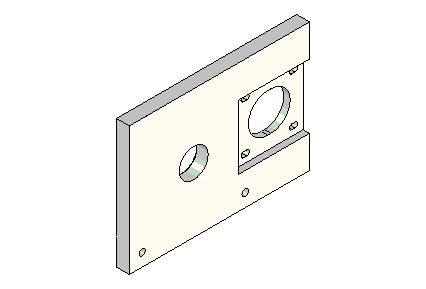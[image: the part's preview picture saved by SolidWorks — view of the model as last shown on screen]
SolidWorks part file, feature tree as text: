
SOLIDWORKS PART (.sldprt)
format: sldprt  version: not decoded by parser v0  size: 434,176 bytes
history: native  units: mm
features: sketch x10, cut_extrude x6, thread x4, extrude x1, hole x1 (+11 scaffold rows collapsed)
feature tree (33):
  scaffold x11  (default folders/planes/origin — collapsed)
  sketch  "Sketch1"  dims[D1=177.8mm D2=127.0mm]
  extrude  "Extrude1"  Depth=12.7mm
  hole  "5/16-18 Tapped Hole1"  Diameter=6.5278mm Depth=22.9235mm
  sketch  "Sketch3"  dims[c1.D1=19.05mm c1.D2=38.1mm c1.D3=38.1mm c1.D4=38.1mm c1.D5=6.35mm c2.D1=31.75mm]
  sketch  "Sketch2"  dims[hole-wizard template sketch: 47 standard entries collapsed; hole parameters kept: c15.Tap Drill Depth=22.9235mm c15.D3=~14.816244mm c15.Drill Angle=118.0deg]
  thread  "Cosmetic Thread1"  Diameter=15.875mm  [1 undecoded]
  thread  "Cosmetic Thread2"  Diameter=15.875mm  [1 undecoded]
  thread  "Cosmetic Thread3"  Diameter=15.875mm  [1 undecoded]
  thread  "Cosmetic Thread4"  Diameter=15.875mm  [1 undecoded]
  sketch  "Sketch4"  dims[c1.D1=115.9256mm c1.D2=31.6992mm c1.D3=30.0736mm c1.D4=25.2222mm c1.D5=64.1604mm c1.D6=57.7088mm c1.D7=57.7088mm c1.D8=30.0736mm c1.D9=30.0736mm c1.D10=64.1604mm c1.D11=64.1604mm c1.D12=25.4mm c1.D13=25.4mm c1.D14=25.4mm c1.D15=25.4mm c1.D16=25.4mm c1.D17=25.4mm c2.D15=25.4mm c2.D11=30.0736mm c2.D18=30.0736mm c2.D19=64.1604mm c2.D2=30.0736mm c2.D5=115.9256mm c2.D7=25.2222mm c2.D8=25.2222mm c2.D9=25.2222mm c2.D6=63.5mm c3.D7=76.2mm c3.D8=30.48mm c3.D9=30.48mm c3.D10=~36.981169mm c3.D11=38.1mm c3.D14=15.875mm c3.D15=25.4mm c3.D16=15.875mm c3.D17=25.4mm c4.D15=25.4mm c4.D11=~78.928619mm c4.D18=79.375mm c4.D19=64.008mm c4.D2=63.5mm c4.D5=82.55mm c4.D7=79.375mm c4.D8=3.175mm c4.D9=63.5mm]
  sketch  "Sketch8"  dims[c1.D3=3.175mm c1.D1=63.5mm c1.D2=63.5mm c2.D1=63.5mm c2.D2=69.85mm c2.D3=63.5mm]
  cut_extrude  "Cut-Extrude2"  Depth=6.35mm
  sketch  "Sketch5"  dims[c1.D1=38.1mm c1.D2=38.1mm c1.D3=38.1mm c2.D2=28.575mm c2.D3=28.575mm]
  cut_extrude  "Cut-Extrude1"  [1 undecoded]
  sketch  "Sketch9"  dims[c1.D1=4.9784mm c1.D3=2.4892mm c1.D4=2.4892mm c1.D2=2.4892mm c2.D3=2.4892mm c2.D4=2.4892mm c2.D5=4.9784mm c2.D6=2.4892mm c2.D7=2.4892mm c2.D8=2.4892mm c2.D9=4.9784mm c2.D10=4.9784mm c2.D11=2.4892mm c2.D12=2.4892mm c2.D13=2.4892mm c2.D14=2.4892mm c2.D15=2.4892mm c2.D16=2.4892mm c2.D2=23.876mm c3.D3=23.876mm c3.D4=23.876mm c3.D2=23.876mm c4.D3=23.876mm c4.D4=23.876mm c4.D6=23.876mm c4.D7=23.876mm c4.D8=23.876mm c4.D11=23.876mm c4.D12=23.876mm c4.D13=23.876mm c4.D14=23.876mm c4.D15=23.876mm c4.D16=23.876mm]
  cut_extrude  "Cut-Extrude4"  [1 undecoded]
  sketch  "Sketch10"  dims[D1=28.575mm]
  cut_extrude  "Cut-Extrude5"  [1 undecoded]
  sketch  "Sketch11"  dims[D1=31.75mm]
  cut_extrude  "Cut-Extrude6"  Depth=1.5875mm
  sketch  "Sketch12"  dims[D1=6.35mm D2=101.6mm D3=12.7mm]
  cut_extrude  "Cut-Extrude7"  [1 undecoded]
decode coverage: 18 of 22 modeling features carry decoded parameters
note: ~ marks probable driven/reference dimensions
note: 8 parameter values undecoded
summary: no parameter record found for 4 features
note: suppression state not decoded; provenance and decode notes live in map.json
